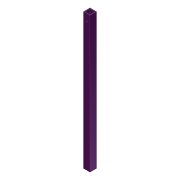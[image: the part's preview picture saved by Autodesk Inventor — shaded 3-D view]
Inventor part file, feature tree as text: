
AUTODESK INVENTOR PART (.ipt)
format: ipt  version: 2012 (Build 160160000, 160)  size: 82,944 bytes
history: native  units: in
note: dims shown in document units (in); Inventor stores cm internally (conversion verified against a paired STEP export)
features: extrude x2, sketch x2, shell x1
ambient origin geometry x8: Origin, YZ Plane, XZ Plane, XY Plane, X Axis, Y Axis, Z Axis, Center Point
bodies: Solid1 (feature_tree)
feature tree (5):
  extrude  "Extrusion1"  Depth=20.5in
  shell  "Shell1"  Thickness=1.0in
  extrude  "Extrusion2"  Depth=0.5in
  sketch  "Sketch1"  dims[d0=1.0in d1=20.5in d2=1.0in d3=0.0in]
  sketch  "Sketch2"  dims[d4=0.125in d5=0.5in d6=1.0in d7=0.25in d8=1.0in d9=0.0in]
